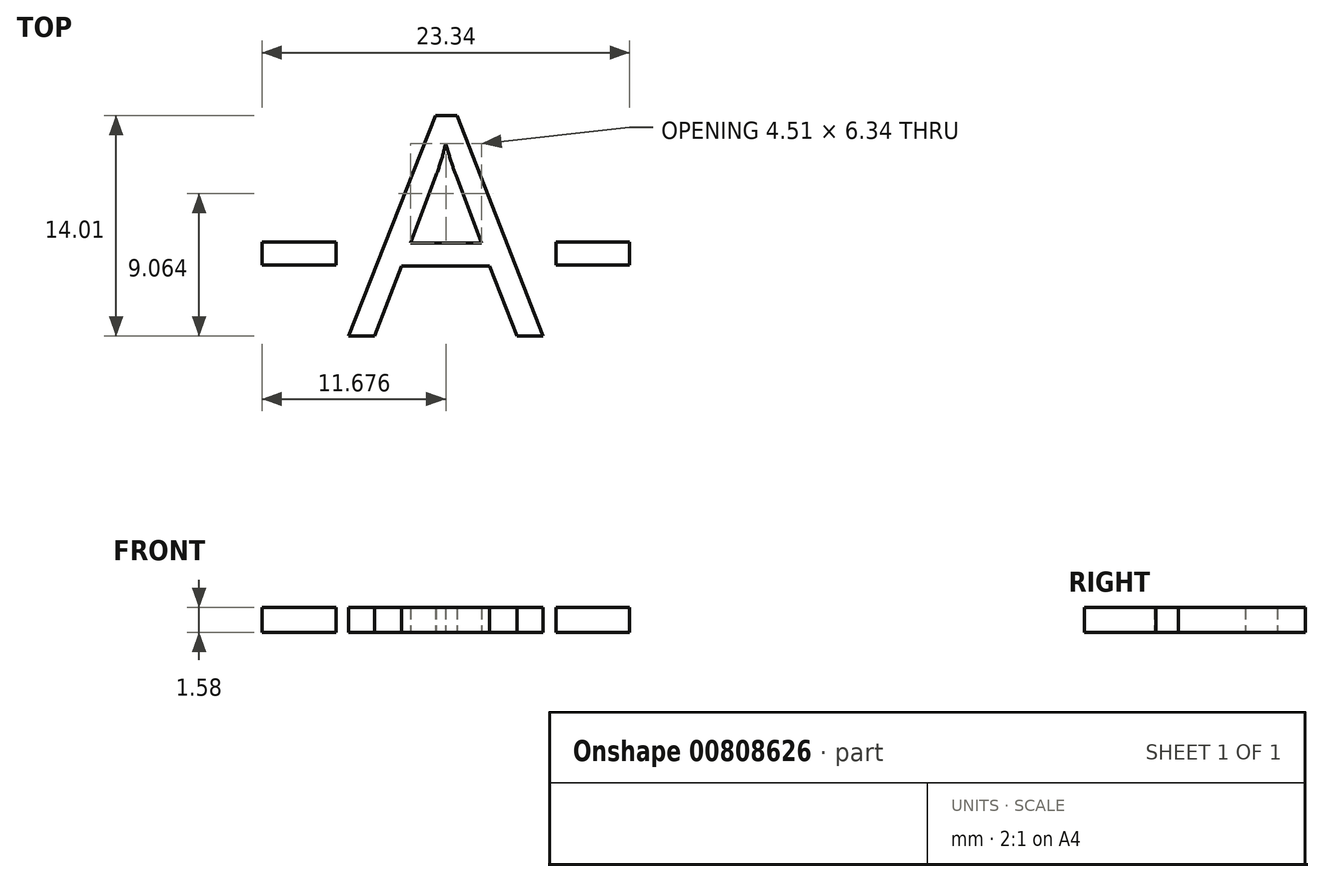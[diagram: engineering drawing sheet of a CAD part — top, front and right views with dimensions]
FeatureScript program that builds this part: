
annotation { "Feature Type Name" : "Feature", "Feature Type Description" : "" }
export const myFeature = defineFeature(function(context is Context, id is Id, definition is map)
    precondition{}
    {
        {
            var Q0;
            Q0=qCreatedBy(makeId("Top.planeOp"),FACE);
            var sketch = newSketch(context, id + "F0", { "sketchPlane" : qUnion([Q0])});
            skText(sketch, "E0", { "text": "-A-", "fontName": "OpenSans-Regular.ttf"});
            const initialGuessF0  = {"E0": [-0.0127, -0.00703, 1, 0, 0.01407]};
            skSetInitialGuess(sketch, initialGuessF0);
            skSolve(sketch);
        }
        {
            var Q0;
            Q0 = qSketchRegion(id + "F0", true);
            extrude(context, id + "F1", {"entities" : qUnion([Q0]), "endBound" : BoundingType.SYMMETRIC, "depth" : 1.59 * mm, "offsetDistance" : 25.4 * mm});
        }
    });
